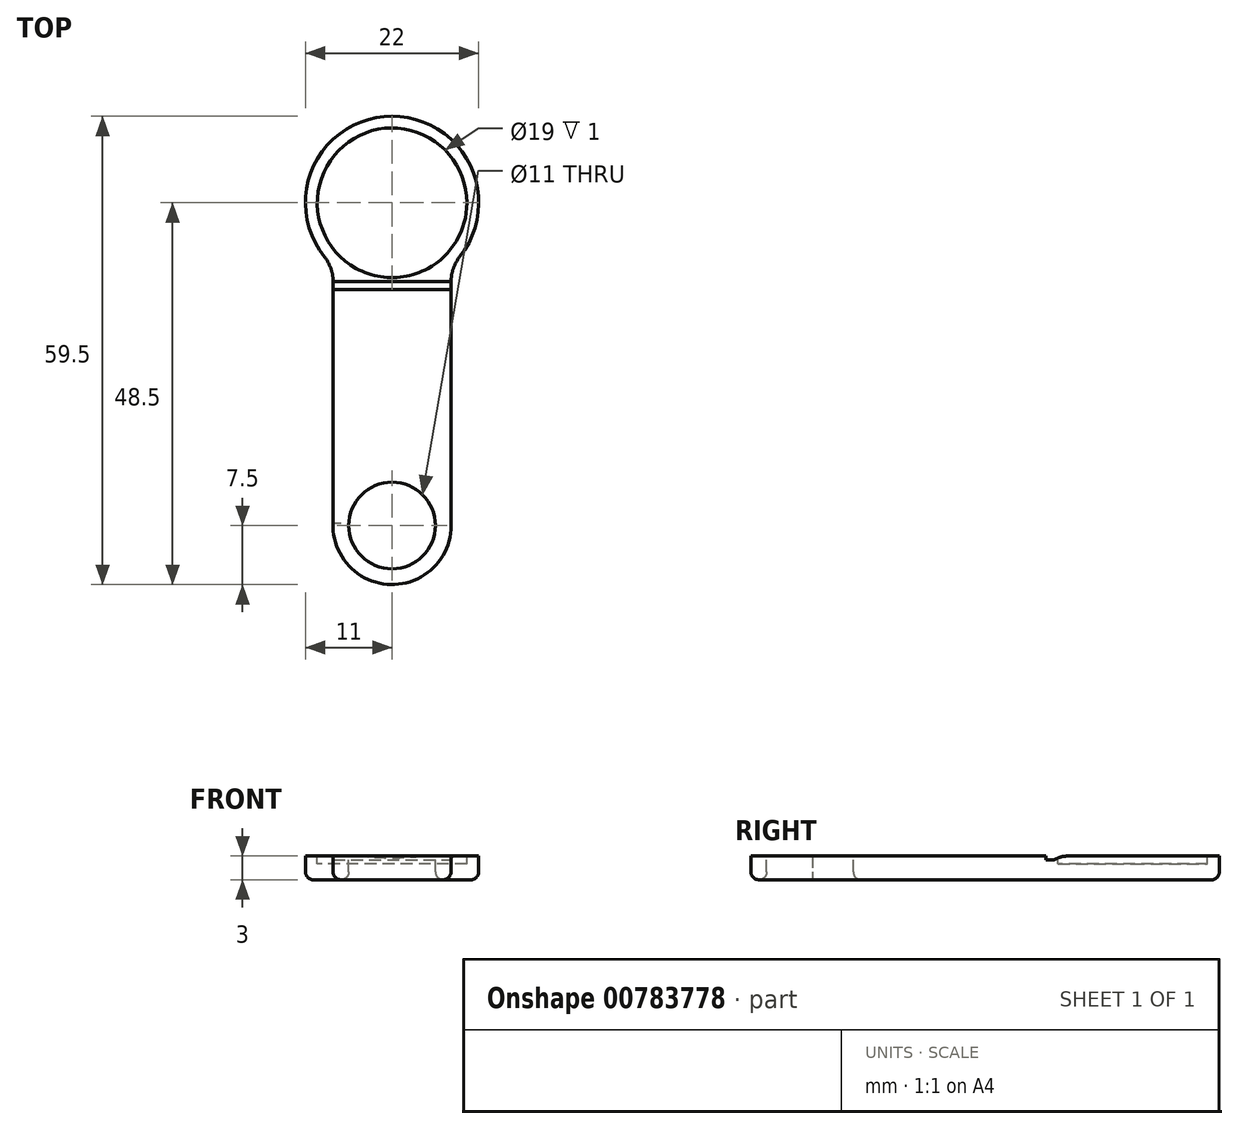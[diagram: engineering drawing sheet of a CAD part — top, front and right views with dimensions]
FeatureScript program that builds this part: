
annotation { "Feature Type Name" : "Feature", "Feature Type Description" : "" }
export const myFeature = defineFeature(function(context is Context, id is Id, definition is map)
    precondition{}
    {
        {
            var Q0;
            Q0=qCreatedBy(makeId("Top.planeOp"),FACE);
            var sketch = newSketch(context, id + "F0", { "sketchPlane" : qUnion([Q0])});
            skArc(sketch, "E0", {"start": v(8.6, -6.87) * mm, "mid": v(0, 11) * mm, "end": v(-8.59, -6.87) * mm});
            skLineSegment(sketch, "E1", {"start": v(0, -11) * mm, "end": v(0, -41) * mm, "construction": true});
            skArc(sketch, "E2", {"start": v(-7.5, -40.67) * mm, "mid": v(-0.16, -48.5) * mm, "end": v(7.5, -41) * mm});
            skLineSegment(sketch, "E3", {"start": v(-7.5, -41.33) * mm, "end": v(-7.5, -10) * mm});
            skLineSegment(sketch, "E4", {"start": v(7.5, -41) * mm, "end": v(7.5, -9.99) * mm});
            skPoint(sketch, "E5.visualSharp", {"position": v(-7.5, -8.05) * mm});
            skArc(sketch, "E5.filletArc", {"start": v(-7.5, -10) * mm, "mid": v(-7.77, -8.34) * mm, "end": v(-8.59, -6.87) * mm});
            skPoint(sketch, "E6.visualSharp", {"position": v(7.5, -8.05) * mm});
            skArc(sketch, "E6.filletArc", {"start": v(8.6, -6.87) * mm, "mid": v(7.78, -8.33) * mm, "end": v(7.5, -9.99) * mm});
            skSolve(sketch);
        }
        {
            var Q0;
            Q0 = qSketchRegion(id + "F0", true);
            extrude(context, id + "F1", {"entities" : qUnion([Q0]), "depth" : 3 * mm, "offsetDistance" : 25 * mm});
        }
        {
            var Q0;
            Q0=makeQuery(id+"F1.opExtrude","CAP_FACE",FACE,{"disambiguationData":[OSD([sQuery(id+"F0.wireOp",EDGE,"E0"),sQuery(id+"F0.wireOp",EDGE,"E2"),sQuery(id+"F0.wireOp",EDGE,"E3"),sQuery(id+"F0.wireOp",EDGE,"E4"),sQuery(id+"F0.wireOp",EDGE,"E5.filletArc"),sQuery(id+"F0.wireOp",EDGE,"E6.filletArc")])],"isStart":false});
            var sketch = newSketch(context, id + "F2", { "sketchPlane" : qUnion([Q0])});
            skCircle(sketch, "E7", {"center": v(0, 0) * mm, "radius": 9.5 * mm});
            skSolve(sketch);
        }
        {
            var Q0;
            Q0 = qSketchRegion(id + "F2", true);
            extrude(context, id + "F3", {"entities" : qUnion([Q0]), "operationType" : NewBodyOperationType.REMOVE, "oppositeDirection" : true, "depth" : 1 * mm, "offsetDistance" : 25 * mm});
        }
        {
            var Q0;
            Q0=makeQuery(id+"F1.opExtrude","CAP_FACE",FACE,{"disambiguationData":[OSD([sQuery(id+"F0.wireOp",EDGE,"E0"),sQuery(id+"F0.wireOp",EDGE,"E2"),sQuery(id+"F0.wireOp",EDGE,"E3"),sQuery(id+"F0.wireOp",EDGE,"E4"),sQuery(id+"F0.wireOp",EDGE,"E5.filletArc"),sQuery(id+"F0.wireOp",EDGE,"E6.filletArc")])],"isStart":false});
            var sketch = newSketch(context, id + "F4", { "sketchPlane" : qUnion([Q0])});
            skLineSegment(sketch, "E8", {"start": v(-7.5, -11) * mm, "end": v(7.5, -11) * mm});
            skLineSegment(sketch, "E9", {"start": v(-7.5, -11) * mm, "end": v(-7.5, -10) * mm});
            skLineSegment(sketch, "E10", {"start": v(-7.5, -10) * mm, "end": v(7.5, -10) * mm});
            skLineSegment(sketch, "E11", {"start": v(7.5, -10) * mm, "end": v(7.5, -11) * mm});
            skSolve(sketch);
        }
        {
            var Q0;
            Q0 = qSketchRegion(id + "F4", true);
            extrude(context, id + "F5", {"entities" : qUnion([Q0]), "operationType" : NewBodyOperationType.REMOVE, "oppositeDirection" : true, "depth" : 0.5 * mm, "offsetDistance" : 25 * mm});
        }
        {
            var Q0;
            Q0=makeQuery(id+"F5.boolean.opBoolean","COPY",EDGE,{"derivedFrom":makeQuery(id+"F5.opExtrude","CAP_EDGE",EDGE,{"disambiguationData":[OSD([sQuery(id+"F4.wireOp",EDGE,"E8")])],"isStart":true})});
            var Q1;
            Q1=makeQuery(id+"F5.boolean.opBoolean","COPY",EDGE,{"derivedFrom":makeQuery(id+"F5.opExtrude","CAP_EDGE",EDGE,{"disambiguationData":[OSD([sQuery(id+"F4.wireOp",EDGE,"E10")])],"isStart":true})});
            fillet(context, id + "F6", {"entities" : qUnion([Q0, Q1]), "radius" : 3 * mm, "tangentPropagation" : true, "allowEdgeOverflow" : false});
        }
        {
            var Q0;
            {var subQ0=sQuery(id+"F0.wireOp",EDGE,"E2");var subQ1=sQuery(id+"F0.wireOp",EDGE,"E3");var subQ2=sQuery(id+"F0.wireOp",EDGE,"E4");Q0=makeQuery(id+"F5.boolean.opBoolean","SPLIT",FACE,{"disambiguationData":[TD([makeQuery(id+"F1.opExtrude","SWEPT_FACE",FACE,{"disambiguationData":[OSD([subQ0])]})])],"derivedFrom":makeQuery(id+"F1.opExtrude","CAP_FACE",FACE,{"disambiguationData":[OSD([sQuery(id+"F0.wireOp",EDGE,"E0"),subQ0,subQ1,subQ2,sQuery(id+"F0.wireOp",EDGE,"E5.filletArc"),sQuery(id+"F0.wireOp",EDGE,"E6.filletArc")])],"isStart":false})});}
            var sketch = newSketch(context, id + "F7", { "sketchPlane" : qUnion([Q0])});
            skCircle(sketch, "E12", {"center": v(0, -41) * mm, "radius": 5.5 * mm});
            skSolve(sketch);
        }
        {
            var Q0;
            Q0 = qSketchRegion(id + "F7", true);
            extrude(context, id + "F8", {"entities" : qUnion([Q0]), "operationType" : NewBodyOperationType.REMOVE, "endBound" : BoundingType.THROUGH_ALL, "oppositeDirection" : true, "depth" : 25 * mm, "offsetDistance" : 25 * mm});
        }
        {
            var Q0;
            Q0=makeQuery(id+"F1.opExtrude","CAP_FACE",FACE,{"disambiguationData":[OSD([sQuery(id+"F0.wireOp",EDGE,"E0"),sQuery(id+"F0.wireOp",EDGE,"E2"),sQuery(id+"F0.wireOp",EDGE,"E3"),sQuery(id+"F0.wireOp",EDGE,"E4"),sQuery(id+"F0.wireOp",EDGE,"E5.filletArc"),sQuery(id+"F0.wireOp",EDGE,"E6.filletArc")])],"isStart":true});
            fillet(context, id + "F9", {"entities" : qUnion([Q0]), "radius" : 1 * mm, "tangentPropagation" : true, "allowEdgeOverflow" : false});
        }
    });
